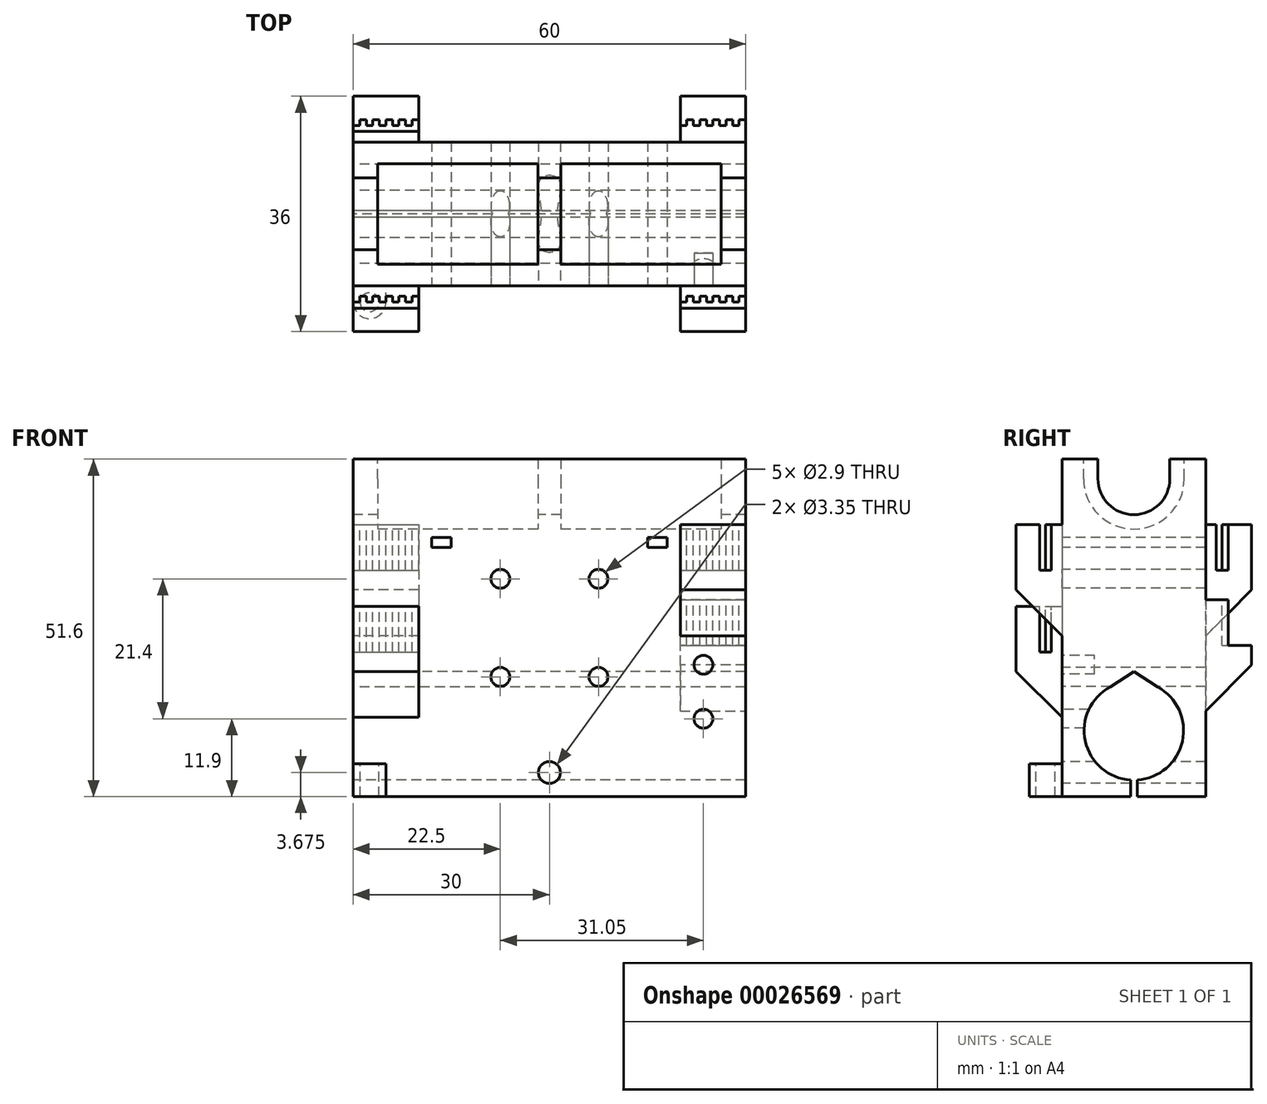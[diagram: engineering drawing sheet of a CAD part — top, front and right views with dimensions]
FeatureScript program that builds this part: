
annotation { "Feature Type Name" : "Feature", "Feature Type Description" : "" }
export const myFeature = defineFeature(function(context is Context, id is Id, definition is map)
    precondition{}
    {
        {
            var Q0;
            Q0=qCreatedBy(makeId("Top.planeOp"),FACE);
            var sketch = newSketch(context, id + "F0", { "sketchPlane" : qUnion([Q0])});
            skLineSegment(sketch, "E0.bottom", {"start": v(0, 0) * mm, "end": v(60, 0) * mm});
            skLineSegment(sketch, "E0.top", {"start": v(0, 22) * mm, "end": v(60, 22) * mm});
            skLineSegment(sketch, "E0.left", {"start": v(0, 0) * mm, "end": v(0, 22) * mm});
            skLineSegment(sketch, "E0.right", {"start": v(60, 0) * mm, "end": v(60, 22) * mm});
            skSolve(sketch);
        }
        {
            var Q0;
            Q0=qSketchRegion(id+"F0",true);
            extrude(context, id + "F1", {"entities" : qUnion([Q0]), "depth" : 51.6 * mm});
        }
        {
            var Q0;
            Q0=makeQuery(id+"F1.opExtrude","SWEPT_FACE",FACE,{"disambiguationData":[OSD([sQuery(id+"F0.wireOp",EDGE,"E0.left")])]});
            var sketch = newSketch(context, id + "F2", { "sketchPlane" : qUnion([Q0])});
            skCircle(sketch, "E1", {"center": v(-11, 10.1) * mm, "radius": 7.6 * mm});
            skCircle(sketch, "E2", {"center": v(-11, 48.6) * mm, "radius": 5.5 * mm});
            skLineSegment(sketch, "E3", {"start": v(-22, 48.6) * mm, "end": v(0, 48.6) * mm, "construction": true});
            skLineSegment(sketch, "E4", {"start": v(-16.5, 51.6) * mm, "end": v(-16.5, 48.6) * mm});
            skLineSegment(sketch, "E5", {"start": v(-5.5, 51.6) * mm, "end": v(-5.5, 48.6) * mm});
            skLineSegment(sketch, "E6", {"start": v(-22, 10.1) * mm, "end": v(0, 10.1) * mm, "construction": true});
            skLineSegment(sketch, "E7", {"start": v(-11, 10.1) * mm, "end": v(-11, 0) * mm, "construction": true});
            skLineSegment(sketch, "E8", {"start": v(-11, 0) * mm, "end": v(-11.5, 0) * mm});
            skLineSegment(sketch, "E9", {"start": v(-11.5, 0) * mm, "end": v(-11.5, 2.52) * mm});
            skLineSegment(sketch, "E10", {"start": v(-11.5, 2.52) * mm, "end": v(-10.5, 2.52) * mm});
            skLineSegment(sketch, "E11", {"start": v(-10.5, 2.52) * mm, "end": v(-10.5, 0) * mm});
            skLineSegment(sketch, "E12", {"start": v(-10.5, 0) * mm, "end": v(-11, 0) * mm});
            skLineSegment(sketch, "E13", {"start": v(-11, 17.7) * mm, "end": v(-11, 19.08) * mm});
            skLineSegment(sketch, "E14", {"start": v(-11, 19.08) * mm, "end": v(-6.5, 16.22) * mm});
            skLineSegment(sketch, "E15", {"start": v(-11, 19.08) * mm, "end": v(-15.5, 16.22) * mm});
            skCircle(sketch, "E16", {"center": v(-11, 48.6) * mm, "radius": 7.7 * mm});
            skLineSegment(sketch, "E17", {"start": v(-3.3, 48.6) * mm, "end": v(-3.3, 51.6) * mm});
            skLineSegment(sketch, "E18", {"start": v(-18.7, 48.6) * mm, "end": v(-18.7, 51.6) * mm});
            skSolve(sketch);
        }
        {
            var Q0;
            {var subQ0=sQuery(id+"F2.wireOp",EDGE,"E14");var subQ1=sQuery(id+"F2.wireOp",EDGE,"E1");var subQ3=makeQuery(id+"F2.imprint","INTERSECT",VERTEX,{"disambiguationData":[OD(0.0)],"derivedFrom":[subQ1,subQ0]});Q0=makeQuery(id+"F2.imprint","IMPRINT",FACE,{"disambiguationData":[TD([[makeQuery(id+"F2.imprint","IMPRINT",EDGE,{"disambiguationData":[TD([[subQ3,-1.0]])],"derivedFrom":subQ1}),1.0]])]});}
            var Q1;
            {var subQ0=sQuery(id+"F2.wireOp",EDGE,"E15");var subQ1=sQuery(id+"F2.wireOp",EDGE,"E1");var subQ3=makeQuery(id+"F2.imprint","INTERSECT",VERTEX,{"disambiguationData":[OD(0.0)],"derivedFrom":[subQ1,subQ0]});Q1=makeQuery(id+"F2.imprint","IMPRINT",FACE,{"disambiguationData":[TD([[makeQuery(id+"F2.imprint","IMPRINT",EDGE,{"disambiguationData":[TD([[subQ3,1.0]])],"derivedFrom":subQ1}),1.0]])]});}
            var Q2;
            Q2=makeQuery(id+"F2.imprint","IMPRINT",FACE,{"disambiguationData":[TD([[makeQuery(id+"F2.imprint","IMPRINT",EDGE,{"derivedFrom":sQuery(id+"F2.wireOp",EDGE,"E8")}),-1.0]])]});
            var Q3;
            {var subQ0=sQuery(id+"F2.wireOp",EDGE,"E10");Q3=makeQuery(id+"F2.imprint","IMPRINT",FACE,{"disambiguationData":[TD([[makeQuery(id+"F2.imprint","IMPRINT",EDGE,{"derivedFrom":subQ0}),-1.0]])]});}
            var Q4;
            {var subQ3=sQuery(id+"F2.wireOp",EDGE,"E13");Q4=makeQuery(id+"F2.imprint","IMPRINT",FACE,{"disambiguationData":[TD([[makeQuery(id+"F2.imprint","IMPRINT",EDGE,{"derivedFrom":subQ3}),-1.0]])]});}
            var Q5;
            {var subQ3=sQuery(id+"F2.wireOp",EDGE,"E13");Q5=makeQuery(id+"F2.imprint","IMPRINT",FACE,{"disambiguationData":[TD([[makeQuery(id+"F2.imprint","IMPRINT",EDGE,{"derivedFrom":subQ3}),1.0]])]});}
            var Q6;
            {var subQ7=sQuery(id+"F2.wireOp",EDGE,"E10");Q6=makeQuery(id+"F2.imprint","IMPRINT",FACE,{"disambiguationData":[TD([[makeQuery(id+"F2.imprint","IMPRINT",EDGE,{"derivedFrom":subQ7}),1.0]])]});}
            var Q7;
            {var subQ3=sQuery(id+"F2.wireOp",EDGE,"E5");Q7=makeQuery(id+"F2.imprint","IMPRINT",FACE,{"disambiguationData":[TD([[makeQuery(id+"F2.imprint","IMPRINT",EDGE,{"derivedFrom":subQ3}),-1.0]])]});}
            var Q8;
            {var subQ0=sQuery(id+"F2.wireOp",EDGE,"E4");Q8=makeQuery(id+"F2.imprint","IMPRINT",FACE,{"disambiguationData":[TD([[makeQuery(id+"F2.imprint","IMPRINT",EDGE,{"derivedFrom":subQ0}),1.0]])]});}
            var Q9;
            {var subQ0=sQuery(id+"F2.wireOp",EDGE,"E4");Q9=makeQuery(id+"F2.imprint","IMPRINT",FACE,{"disambiguationData":[TD([[makeQuery(id+"F2.imprint","IMPRINT",EDGE,{"derivedFrom":subQ0}),1.0]])]});}
            var Q10;
            {var subQ3=sQuery(id+"F2.wireOp",EDGE,"E5");Q10=makeQuery(id+"F2.imprint","IMPRINT",FACE,{"disambiguationData":[TD([[makeQuery(id+"F2.imprint","IMPRINT",EDGE,{"derivedFrom":subQ3}),-1.0]])]});}
            var Q11;
            {var subQ1=sQuery(id+"F2.wireOp",EDGE,"E2");var subQ4=makeQuery(id+"F2.imprint","INTERSECT",VERTEX,{"derivedFrom":[subQ1,sQuery(id+"F2.wireOp",EDGE,"E5")]});Q11=makeQuery(id+"F2.imprint","IMPRINT",FACE,{"disambiguationData":[TD([[makeQuery(id+"F2.imprint","IMPRINT",EDGE,{"disambiguationData":[TD([[subQ4,-1.0]])],"derivedFrom":subQ1}),1.0]])]});}
            extrude(context, id + "F3", {"entities" : qUnion([Q0, Q1, Q2, Q3, Q4, Q5, Q6, Q7, Q8, Q9, Q10, Q11]), "operationType" : NewBodyOperationType.REMOVE, "endBound" : BoundingType.THROUGH_ALL, "oppositeDirection" : true, "depth" : 25 * mm});
        }
        {
            var Q0;
            {var subQ3=sQuery(id+"F2.wireOp",EDGE,"E4");Q0=makeQuery(id+"F2.imprint","IMPRINT",FACE,{"disambiguationData":[TD([[makeQuery(id+"F2.imprint","IMPRINT",EDGE,{"derivedFrom":subQ3}),-1.0]])]});}
            var Q1;
            {var subQ3=sQuery(id+"F2.wireOp",EDGE,"E18");Q1=makeQuery(id+"F2.imprint","IMPRINT",FACE,{"disambiguationData":[TD([[makeQuery(id+"F2.imprint","IMPRINT",EDGE,{"derivedFrom":subQ3}),-1.0]])]});}
            var Q2;
            {var subQ3=sQuery(id+"F2.wireOp",EDGE,"E17");Q2=makeQuery(id+"F2.imprint","IMPRINT",FACE,{"disambiguationData":[TD([[makeQuery(id+"F2.imprint","IMPRINT",EDGE,{"derivedFrom":subQ3}),1.0]])]});}
            extrude(context, id + "F4", {"entities" : qUnion([Q0, Q1, Q2]), "operationType" : NewBodyOperationType.REMOVE, "oppositeDirection" : true, "depth" : 56.25 * mm});
        }
        {
            var Q0;
            {var subQ3=sQuery(id+"F2.wireOp",EDGE,"E4");Q0=makeQuery(id+"F2.imprint","IMPRINT",FACE,{"disambiguationData":[TD([[makeQuery(id+"F2.imprint","IMPRINT",EDGE,{"derivedFrom":subQ3}),-1.0]])]});}
            var Q1;
            {var subQ3=sQuery(id+"F2.wireOp",EDGE,"E18");Q1=makeQuery(id+"F2.imprint","IMPRINT",FACE,{"disambiguationData":[TD([[makeQuery(id+"F2.imprint","IMPRINT",EDGE,{"derivedFrom":subQ3}),-1.0]])]});}
            var Q2;
            {var subQ3=sQuery(id+"F2.wireOp",EDGE,"E17");Q2=makeQuery(id+"F2.imprint","IMPRINT",FACE,{"disambiguationData":[TD([[makeQuery(id+"F2.imprint","IMPRINT",EDGE,{"derivedFrom":subQ3}),1.0]])]});}
            extrude(context, id + "F5", {"entities" : qUnion([Q0, Q1, Q2]), "operationType" : NewBodyOperationType.ADD, "oppositeDirection" : true, "depth" : 31.75 * mm});
        }
        {
            var Q0;
            {var subQ3=sQuery(id+"F2.wireOp",EDGE,"E4");Q0=makeQuery(id+"F2.imprint","IMPRINT",FACE,{"disambiguationData":[TD([[makeQuery(id+"F2.imprint","IMPRINT",EDGE,{"derivedFrom":subQ3}),-1.0]])]});}
            var Q1;
            {var subQ3=sQuery(id+"F2.wireOp",EDGE,"E18");Q1=makeQuery(id+"F2.imprint","IMPRINT",FACE,{"disambiguationData":[TD([[makeQuery(id+"F2.imprint","IMPRINT",EDGE,{"derivedFrom":subQ3}),-1.0]])]});}
            var Q2;
            {var subQ3=sQuery(id+"F2.wireOp",EDGE,"E17");Q2=makeQuery(id+"F2.imprint","IMPRINT",FACE,{"disambiguationData":[TD([[makeQuery(id+"F2.imprint","IMPRINT",EDGE,{"derivedFrom":subQ3}),1.0]])]});}
            extrude(context, id + "F6", {"entities" : qUnion([Q0, Q1, Q2]), "operationType" : NewBodyOperationType.REMOVE, "oppositeDirection" : true, "depth" : 28.25 * mm});
        }
        {
            var Q0;
            {var subQ3=sQuery(id+"F2.wireOp",EDGE,"E4");Q0=makeQuery(id+"F2.imprint","IMPRINT",FACE,{"disambiguationData":[TD([[makeQuery(id+"F2.imprint","IMPRINT",EDGE,{"derivedFrom":subQ3}),-1.0]])]});}
            var Q1;
            {var subQ3=sQuery(id+"F2.wireOp",EDGE,"E18");Q1=makeQuery(id+"F2.imprint","IMPRINT",FACE,{"disambiguationData":[TD([[makeQuery(id+"F2.imprint","IMPRINT",EDGE,{"derivedFrom":subQ3}),-1.0]])]});}
            var Q2;
            {var subQ3=sQuery(id+"F2.wireOp",EDGE,"E17");Q2=makeQuery(id+"F2.imprint","IMPRINT",FACE,{"disambiguationData":[TD([[makeQuery(id+"F2.imprint","IMPRINT",EDGE,{"derivedFrom":subQ3}),1.0]])]});}
            extrude(context, id + "F7", {"entities" : qUnion([Q0, Q1, Q2]), "operationType" : NewBodyOperationType.ADD, "oppositeDirection" : true, "depth" : 3.75 * mm});
        }
        {
            var Q0;
            Q0=makeQuery(id+"F1.opExtrude","SWEPT_FACE",FACE,{"disambiguationData":[OSD([sQuery(id+"F0.wireOp",EDGE,"E0.bottom")])]});
            var sketch = newSketch(context, id + "F8", { "sketchPlane" : qUnion([Q0])});
            skLineSegment(sketch, "E19.bottom", {"start": v(0, 29.1) * mm, "end": v(10, 29.1) * mm});
            skLineSegment(sketch, "E19.top", {"start": v(0, 9.1) * mm, "end": v(10, 9.1) * mm});
            skLineSegment(sketch, "E19.left", {"start": v(0, 29.1) * mm, "end": v(0, 9.1) * mm});
            skLineSegment(sketch, "E19.right", {"start": v(10, 29.1) * mm, "end": v(10, 9.1) * mm});
            skLineSegment(sketch, "E20.bottom", {"start": v(60, 41.6) * mm, "end": v(50, 41.6) * mm});
            skLineSegment(sketch, "E20.top", {"start": v(60, 21.6) * mm, "end": v(50, 21.6) * mm});
            skLineSegment(sketch, "E20.left", {"start": v(60, 41.6) * mm, "end": v(60, 21.6) * mm});
            skLineSegment(sketch, "E20.right", {"start": v(50, 41.6) * mm, "end": v(50, 21.6) * mm});
            skPoint(sketch, "E21", {"position": v(0, 48.6) * mm});
            skPoint(sketch, "E22", {"position": v(0, 8.6) * mm});
            skSolve(sketch);
        }
        {
            var Q0;
            Q0=qSketchRegion(id+"F8",true);
            extrude(context, id + "F9", {"entities" : qUnion([Q0]), "operationType" : NewBodyOperationType.ADD, "depth" : 7 * mm});
        }
        {
            var Q0;
            Q0=makeQuery(id+"F9.opExtrude","CAP_EDGE",EDGE,{"disambiguationData":[OSD([sQuery(id+"F8.wireOp",EDGE,"E19.top")])],"isStart":false});
            var Q1;
            Q1=makeQuery(id+"F9.opExtrude","CAP_EDGE",EDGE,{"disambiguationData":[OSD([sQuery(id+"F8.wireOp",EDGE,"E20.top")])],"isStart":false});
            chamfer(context, id + "F10", {"entities" : qUnion([Q0, Q1]), "width" : 10 * mm, "tangentPropagation" : true});
        }
        {
            var Q0;
            Q0=makeQuery(id+"F9.opExtrude","SWEPT_FACE",FACE,{"disambiguationData":[OSD([sQuery(id+"F8.wireOp",EDGE,"E19.bottom")])]});
            var sketch = newSketch(context, id + "F11", { "sketchPlane" : qUnion([Q0])});
            skLineSegment(sketch, "E23", {"start": v(-935.9, 0) * mm, "end": v(-935.88, -4.54) * mm});
            skLineSegment(sketch, "E24.left", {"start": v(0, -3.4) * mm, "end": v(0, -1.6) * mm});
            skLineSegment(sketch, "E25", {"start": v(6, -2.5) * mm, "end": v(7, -2.5) * mm});
            skLineSegment(sketch, "E26", {"start": v(4, -2.5) * mm, "end": v(5, -2.5) * mm});
            skLineSegment(sketch, "E27", {"start": v(0, -2.5) * mm, "end": v(1, -2.5) * mm});
            skLineSegment(sketch, "E28", {"start": v(7, -1.6) * mm, "end": v(8, -1.6) * mm});
            skLineSegment(sketch, "E29", {"start": v(2, -2.5) * mm, "end": v(3, -2.5) * mm});
            skLineSegment(sketch, "E30", {"start": v(3, -1.6) * mm, "end": v(4, -1.6) * mm});
            skLineSegment(sketch, "E31", {"start": v(8, -2.5) * mm, "end": v(9, -2.5) * mm});
            skLineSegment(sketch, "E32", {"start": v(8, -1.6) * mm, "end": v(8, -2.5) * mm});
            skLineSegment(sketch, "E33", {"start": v(9, -2.5) * mm, "end": v(9, -1.6) * mm});
            skLineSegment(sketch, "E34", {"start": v(10, -1.6) * mm, "end": v(10, -2.5) * mm});
            skLineSegment(sketch, "E35", {"start": v(6, -1.6) * mm, "end": v(6, -2.5) * mm});
            skLineSegment(sketch, "E36", {"start": v(2, -1.6) * mm, "end": v(2, -2.5) * mm});
            skLineSegment(sketch, "E37", {"start": v(1, -1.6) * mm, "end": v(2, -1.6) * mm});
            skLineSegment(sketch, "E38", {"start": v(1, -2.5) * mm, "end": v(1, -1.6) * mm});
            skLineSegment(sketch, "E39", {"start": v(9, -1.6) * mm, "end": v(10, -1.6) * mm});
            skLineSegment(sketch, "E40", {"start": v(5, -1.6) * mm, "end": v(6, -1.6) * mm});
            skLineSegment(sketch, "E41", {"start": v(5, -2.5) * mm, "end": v(5, -1.6) * mm});
            skLineSegment(sketch, "E42", {"start": v(3, -2.5) * mm, "end": v(3, -1.6) * mm});
            skLineSegment(sketch, "E43", {"start": v(4, -1.6) * mm, "end": v(4, -2.5) * mm});
            skLineSegment(sketch, "E44", {"start": v(7, -2.5) * mm, "end": v(7, -1.6) * mm});
            skLineSegment(sketch, "E45", {"start": v(0, -1.6) * mm, "end": v(0, -2.5) * mm});
            skLineSegment(sketch, "E46", {"start": v(10, -2.5) * mm, "end": v(10, -3.4) * mm});
            skLineSegment(sketch, "E47", {"start": v(0, -3.4) * mm, "end": v(10, -3.4) * mm});
            skLineSegment(sketch, "E48", {"start": v(5.3, -1.6) * mm, "end": v(5.3, 0) * mm});
            skSolve(sketch);
        }
        {
            var Q0;
            Q0=qSketchRegion(id+"F11",true);
            extrude(context, id + "F12", {"entities" : qUnion([Q0]), "operationType" : NewBodyOperationType.REMOVE, "oppositeDirection" : true, "depth" : 7 * mm});
        }
        {
            var Q0;
            Q0=makeQuery(id+"F9.opExtrude","SWEPT_FACE",FACE,{"disambiguationData":[OSD([sQuery(id+"F8.wireOp",EDGE,"E20.bottom")])]});
            var sketch = newSketch(context, id + "F13", { "sketchPlane" : qUnion([Q0])});
            skLineSegment(sketch, "E49.left", {"start": v(50, -3.4) * mm, "end": v(50, -1.6) * mm});
            skLineSegment(sketch, "E50", {"start": v(56, -2.5) * mm, "end": v(57, -2.5) * mm});
            skLineSegment(sketch, "E51", {"start": v(54, -2.5) * mm, "end": v(55, -2.5) * mm});
            skLineSegment(sketch, "E52", {"start": v(50, -2.5) * mm, "end": v(51, -2.5) * mm});
            skLineSegment(sketch, "E53", {"start": v(57, -1.6) * mm, "end": v(58, -1.6) * mm});
            skLineSegment(sketch, "E54", {"start": v(52, -2.5) * mm, "end": v(53, -2.5) * mm});
            skLineSegment(sketch, "E55", {"start": v(53, -1.6) * mm, "end": v(54, -1.6) * mm});
            skLineSegment(sketch, "E56", {"start": v(58, -2.5) * mm, "end": v(59, -2.5) * mm});
            skLineSegment(sketch, "E57", {"start": v(58, -1.6) * mm, "end": v(58, -2.5) * mm});
            skLineSegment(sketch, "E58", {"start": v(59, -2.5) * mm, "end": v(59, -1.6) * mm});
            skLineSegment(sketch, "E59", {"start": v(60, -1.6) * mm, "end": v(60, -2.5) * mm});
            skLineSegment(sketch, "E60", {"start": v(56, -1.6) * mm, "end": v(56, -2.5) * mm});
            skLineSegment(sketch, "E61", {"start": v(52, -1.6) * mm, "end": v(52, -2.5) * mm});
            skLineSegment(sketch, "E62", {"start": v(51, -1.6) * mm, "end": v(52, -1.6) * mm});
            skLineSegment(sketch, "E63", {"start": v(51, -2.5) * mm, "end": v(51, -1.6) * mm});
            skLineSegment(sketch, "E64", {"start": v(59, -1.6) * mm, "end": v(60, -1.6) * mm});
            skLineSegment(sketch, "E65", {"start": v(55, -1.6) * mm, "end": v(56, -1.6) * mm});
            skLineSegment(sketch, "E66", {"start": v(55, -2.5) * mm, "end": v(55, -1.6) * mm});
            skLineSegment(sketch, "E67", {"start": v(53, -2.5) * mm, "end": v(53, -1.6) * mm});
            skLineSegment(sketch, "E68", {"start": v(54, -1.6) * mm, "end": v(54, -2.5) * mm});
            skLineSegment(sketch, "E69", {"start": v(57, -2.5) * mm, "end": v(57, -1.6) * mm});
            skLineSegment(sketch, "E70", {"start": v(50, -1.6) * mm, "end": v(50, -2.5) * mm});
            skLineSegment(sketch, "E71", {"start": v(60, -2.5) * mm, "end": v(60, -3.4) * mm});
            skLineSegment(sketch, "E72", {"start": v(50, -3.4) * mm, "end": v(60, -3.4) * mm});
            skLineSegment(sketch, "E73", {"start": v(55.23, -1.6) * mm, "end": v(55.23, 0) * mm});
            skSolve(sketch);
        }
        {
            var Q0;
            Q0=qSketchRegion(id+"F13",true);
            extrude(context, id + "F14", {"entities" : qUnion([Q0]), "operationType" : NewBodyOperationType.REMOVE, "oppositeDirection" : true, "depth" : 7 * mm});
        }
        {
            var Q0;
            Q0=makeQuery(id+"F1.opExtrude","SWEPT_FACE",FACE,{"disambiguationData":[OSD([sQuery(id+"F0.wireOp",EDGE,"E0.top")])]});
            var sketch = newSketch(context, id + "F15", { "sketchPlane" : qUnion([Q0])});
            skLineSegment(sketch, "E74.bottom", {"start": v(-60, 10.1) * mm, "end": v(-50, 10.1) * mm});
            skLineSegment(sketch, "E74.top", {"start": v(-60, 30.1) * mm, "end": v(-50, 30.1) * mm});
            skLineSegment(sketch, "E74.left", {"start": v(-60, 10.1) * mm, "end": v(-60, 30.1) * mm});
            skLineSegment(sketch, "E74.right", {"start": v(-50, 10.1) * mm, "end": v(-50, 30.1) * mm});
            skLineSegment(sketch, "E75.bottom", {"start": v(0, 41.6) * mm, "end": v(-10, 41.6) * mm});
            skLineSegment(sketch, "E75.top", {"start": v(0, 21.6) * mm, "end": v(-10, 21.6) * mm});
            skLineSegment(sketch, "E75.left", {"start": v(0, 41.6) * mm, "end": v(0, 21.6) * mm});
            skLineSegment(sketch, "E75.right", {"start": v(-10, 41.6) * mm, "end": v(-10, 21.6) * mm});
            skSolve(sketch);
        }
        {
            var Q0;
            Q0=qSketchRegion(id+"F15",true);
            extrude(context, id + "F16", {"entities" : qUnion([Q0]), "operationType" : NewBodyOperationType.ADD, "depth" : 7 * mm});
        }
        {
            var Q0;
            Q0=makeQuery(id+"F16.opExtrude","SWEPT_FACE",FACE,{"disambiguationData":[OSD([sQuery(id+"F15.wireOp",EDGE,"E74.top")])]});
            var sketch = newSketch(context, id + "F17", { "sketchPlane" : qUnion([Q0])});
            skLineSegment(sketch, "E76.left", {"start": v(50, 23.6) * mm, "end": v(50, 25.4) * mm});
            skLineSegment(sketch, "E77", {"start": v(56, 24.5) * mm, "end": v(57, 24.5) * mm});
            skLineSegment(sketch, "E78", {"start": v(54, 24.5) * mm, "end": v(55, 24.5) * mm});
            skLineSegment(sketch, "E79", {"start": v(50, 24.5) * mm, "end": v(51, 24.5) * mm});
            skLineSegment(sketch, "E80", {"start": v(57, 25.4) * mm, "end": v(58, 25.4) * mm});
            skLineSegment(sketch, "E81", {"start": v(52, 24.5) * mm, "end": v(53, 24.5) * mm});
            skLineSegment(sketch, "E82", {"start": v(53, 25.4) * mm, "end": v(54, 25.4) * mm});
            skLineSegment(sketch, "E83", {"start": v(58, 24.5) * mm, "end": v(59, 24.5) * mm});
            skLineSegment(sketch, "E84", {"start": v(58, 25.4) * mm, "end": v(58, 24.5) * mm});
            skLineSegment(sketch, "E85", {"start": v(59, 24.5) * mm, "end": v(59, 25.4) * mm});
            skLineSegment(sketch, "E86", {"start": v(60, 25.4) * mm, "end": v(60, 24.5) * mm});
            skLineSegment(sketch, "E87", {"start": v(56, 25.4) * mm, "end": v(56, 24.5) * mm});
            skLineSegment(sketch, "E88", {"start": v(52, 25.4) * mm, "end": v(52, 24.5) * mm});
            skLineSegment(sketch, "E89", {"start": v(51, 25.4) * mm, "end": v(52, 25.4) * mm});
            skLineSegment(sketch, "E90", {"start": v(51, 24.5) * mm, "end": v(51, 25.4) * mm});
            skLineSegment(sketch, "E91", {"start": v(59, 25.4) * mm, "end": v(60, 25.4) * mm});
            skLineSegment(sketch, "E92", {"start": v(55, 25.4) * mm, "end": v(56, 25.4) * mm});
            skLineSegment(sketch, "E93", {"start": v(55, 24.5) * mm, "end": v(55, 25.4) * mm});
            skLineSegment(sketch, "E94", {"start": v(53, 24.5) * mm, "end": v(53, 25.4) * mm});
            skLineSegment(sketch, "E95", {"start": v(54, 25.4) * mm, "end": v(54, 24.5) * mm});
            skLineSegment(sketch, "E96", {"start": v(57, 24.5) * mm, "end": v(57, 25.4) * mm});
            skLineSegment(sketch, "E97", {"start": v(50, 25.4) * mm, "end": v(50, 24.5) * mm});
            skLineSegment(sketch, "E98", {"start": v(60, 24.5) * mm, "end": v(60, 23.6) * mm});
            skLineSegment(sketch, "E99", {"start": v(50, 23.6) * mm, "end": v(60, 23.6) * mm});
            skLineSegment(sketch, "E100", {"start": v(55, 23.6) * mm, "end": v(55, 22) * mm});
            skSolve(sketch);
        }
        {
            var Q0;
            {var subQ4=sQuery(id+"F17.wireOp",EDGE,"E76.left");Q0=makeQuery(id+"F17.imprint","IMPRINT",FACE,{"disambiguationData":[TD([[makeQuery(id+"F17.imprint","IMPRINT",EDGE,{"derivedFrom":subQ4}),1.0]])]});}
            extrude(context, id + "F18", {"entities" : qUnion([Q0]), "operationType" : NewBodyOperationType.REMOVE, "oppositeDirection" : true, "depth" : 7 * mm});
        }
        {
            var Q0;
            Q0=makeQuery(id+"F16.opExtrude","SWEPT_FACE",FACE,{"disambiguationData":[OSD([sQuery(id+"F15.wireOp",EDGE,"E75.bottom")])]});
            var sketch = newSketch(context, id + "F19", { "sketchPlane" : qUnion([Q0])});
            skLineSegment(sketch, "E101", {"start": v(6, 24.5) * mm, "end": v(7, 24.5) * mm});
            skLineSegment(sketch, "E102", {"start": v(4, 24.5) * mm, "end": v(5, 24.5) * mm});
            skLineSegment(sketch, "E103", {"start": v(0, 24.5) * mm, "end": v(1, 24.5) * mm});
            skLineSegment(sketch, "E104", {"start": v(7, 25.4) * mm, "end": v(8, 25.4) * mm});
            skLineSegment(sketch, "E105", {"start": v(2, 24.5) * mm, "end": v(3, 24.5) * mm});
            skLineSegment(sketch, "E106", {"start": v(3, 25.4) * mm, "end": v(4, 25.4) * mm});
            skLineSegment(sketch, "E107", {"start": v(8, 24.5) * mm, "end": v(9, 24.5) * mm});
            skLineSegment(sketch, "E108", {"start": v(8, 25.4) * mm, "end": v(8, 24.5) * mm});
            skLineSegment(sketch, "E109", {"start": v(9, 24.5) * mm, "end": v(9, 25.4) * mm});
            skLineSegment(sketch, "E110", {"start": v(10, 25.4) * mm, "end": v(10, 24.5) * mm});
            skLineSegment(sketch, "E111", {"start": v(6, 25.4) * mm, "end": v(6, 24.5) * mm});
            skLineSegment(sketch, "E112", {"start": v(2, 25.4) * mm, "end": v(2, 24.5) * mm});
            skLineSegment(sketch, "E113", {"start": v(1, 25.4) * mm, "end": v(2, 25.4) * mm});
            skLineSegment(sketch, "E114", {"start": v(1, 24.5) * mm, "end": v(1, 25.4) * mm});
            skLineSegment(sketch, "E115", {"start": v(9, 25.4) * mm, "end": v(10, 25.4) * mm});
            skLineSegment(sketch, "E116", {"start": v(5, 25.4) * mm, "end": v(6, 25.4) * mm});
            skLineSegment(sketch, "E117", {"start": v(5, 24.5) * mm, "end": v(5, 25.4) * mm});
            skLineSegment(sketch, "E118", {"start": v(3, 24.5) * mm, "end": v(3, 25.4) * mm});
            skLineSegment(sketch, "E119", {"start": v(4, 25.4) * mm, "end": v(4, 24.5) * mm});
            skLineSegment(sketch, "E120", {"start": v(7, 24.5) * mm, "end": v(7, 25.4) * mm});
            skLineSegment(sketch, "E121", {"start": v(10, 24.5) * mm, "end": v(10, 23.6) * mm});
            skLineSegment(sketch, "E122", {"start": v(0, 23.6) * mm, "end": v(10, 23.6) * mm});
            skLineSegment(sketch, "E123", {"start": v(5, 23.6) * mm, "end": v(5, 22) * mm});
            skLineSegment(sketch, "E124", {"start": v(0, 23.6) * mm, "end": v(0, 24.5) * mm});
            skSolve(sketch);
        }
        {
            var Q0;
            Q0=makeQuery(id+"F19.imprint","IMPRINT",FACE,{"disambiguationData":[TD([[makeQuery(id+"F19.imprint","IMPRINT",EDGE,{"derivedFrom":sQuery(id+"F19.wireOp",EDGE,"E101")}),-1.0]])]});
            extrude(context, id + "F20", {"entities" : qUnion([Q0]), "operationType" : NewBodyOperationType.REMOVE, "oppositeDirection" : true, "depth" : 7 * mm});
        }
        {
            var Q0;
            Q0=makeQuery(id+"F16.opExtrude","CAP_EDGE",EDGE,{"disambiguationData":[OSD([sQuery(id+"F15.wireOp",EDGE,"E75.top")])],"isStart":false});
            var Q1;
            Q1=makeQuery(id+"F16.opExtrude","CAP_EDGE",EDGE,{"disambiguationData":[OSD([sQuery(id+"F15.wireOp",EDGE,"E74.bottom")])],"isStart":false});
            chamfer(context, id + "F21", {"entities" : qUnion([Q0, Q1]), "width" : 10 * mm, "tangentPropagation" : true});
        }
        {
            var Q0;
            Q0=makeQuery(id+"F1.opExtrude","SWEPT_FACE",FACE,{"disambiguationData":[OSD([sQuery(id+"F0.wireOp",EDGE,"E0.bottom")])]});
            var sketch = newSketch(context, id + "F22", { "sketchPlane" : qUnion([Q0])});
            skCircle(sketch, "E125", {"center": v(22.5, 33.3) * mm, "radius": 1.45 * mm});
            skCircle(sketch, "E126", {"center": v(37.5, 33.3) * mm, "radius": 1.45 * mm});
            skCircle(sketch, "E127", {"center": v(22.5, 18.3) * mm, "radius": 1.45 * mm});
            skCircle(sketch, "E128", {"center": v(37.5, 18.3) * mm, "radius": 1.45 * mm});
            skLineSegment(sketch, "E129", {"start": v(22.5, 33.3) * mm, "end": v(0, 33.3) * mm});
            skLineSegment(sketch, "E130", {"start": v(37.5, 18.3) * mm, "end": v(60, 18.3) * mm});
            skLineSegment(sketch, "E131", {"start": v(37.5, 33.3) * mm, "end": v(37.5, 51.6) * mm});
            skLineSegment(sketch, "E132", {"start": v(22.5, 18.3) * mm, "end": v(22.5, 0) * mm});
            skCircle(sketch, "E133", {"center": v(30, 3.68) * mm, "radius": 1.68 * mm});
            skLineSegment(sketch, "E134", {"start": v(30, 0) * mm, "end": v(30, 13.82) * mm, "construction": true});
            skSolve(sketch);
        }
        {
            var Q0;
            Q0=qSketchRegion(id+"F22",true);
            var Q1;
            Q1=makeQuery(id+"F22.imprint","IMPRINT",FACE,{"disambiguationData":[TD([[makeQuery(id+"F22.imprint","IMPRINT",EDGE,{"derivedFrom":sQuery(id+"F22.wireOp",EDGE,"E125")}),1.0]])]});
            var Q2;
            Q2=makeQuery(id+"F22.imprint","IMPRINT",FACE,{"disambiguationData":[TD([[makeQuery(id+"F22.imprint","IMPRINT",EDGE,{"derivedFrom":sQuery(id+"F22.wireOp",EDGE,"E126")}),1.0]])]});
            var Q3;
            Q3=makeQuery(id+"F22.imprint","IMPRINT",FACE,{"disambiguationData":[TD([[makeQuery(id+"F22.imprint","IMPRINT",EDGE,{"derivedFrom":sQuery(id+"F22.wireOp",EDGE,"E128")}),1.0]])]});
            var Q4;
            Q4=makeQuery(id+"F22.imprint","IMPRINT",FACE,{"disambiguationData":[TD([[makeQuery(id+"F22.imprint","IMPRINT",EDGE,{"derivedFrom":sQuery(id+"F22.wireOp",EDGE,"E127")}),1.0]])]});
            extrude(context, id + "F23", {"entities" : qUnion([Q0, Q1, Q2, Q3, Q4]), "operationType" : NewBodyOperationType.REMOVE, "endBound" : BoundingType.THROUGH_ALL, "oppositeDirection" : true, "depth" : 25 * mm});
        }
        {
            var Q0;
            Q0=makeQuery(id+"F1.opExtrude","SWEPT_FACE",FACE,{"disambiguationData":[OSD([sQuery(id+"F0.wireOp",EDGE,"E0.bottom")])]});
            var sketch = newSketch(context, id + "F24", { "sketchPlane" : qUnion([Q0])});
            skCircle(sketch, "E135", {"center": v(53.55, 20.15) * mm, "radius": 1.45 * mm});
            skCircle(sketch, "E136", {"center": v(53.55, 11.9) * mm, "radius": 1.45 * mm});
            skSolve(sketch);
        }
        {
            var Q0;
            Q0=qSketchRegion(id+"F24",true);
            extrude(context, id + "F25", {"entities" : qUnion([Q0]), "operationType" : NewBodyOperationType.REMOVE, "oppositeDirection" : true, "depth" : 5 * mm});
        }
        {
            var Q0;
            Q0=makeQuery(id+"F1.opExtrude","SWEPT_FACE",FACE,{"disambiguationData":[OSD([sQuery(id+"F0.wireOp",EDGE,"E0.bottom")])]});
            var sketch = newSketch(context, id + "F26", { "sketchPlane" : qUnion([Q0])});
            skText(sketch, "E137", { "text": "F", "fontName": "OpenSans-Bold.ttf"});
            skLineSegment(sketch, "E138", {"start": v(22.5, 33.3) * mm, "end": v(22.5, 18.3) * mm, "construction": true});
            skLineSegment(sketch, "E139", {"start": v(22.5, 18.3) * mm, "end": v(37.5, 18.3) * mm, "construction": true});
            skLineSegment(sketch, "E140", {"start": v(37.5, 18.3) * mm, "end": v(37.5, 33.3) * mm, "construction": true});
            skLineSegment(sketch, "E141", {"start": v(37.5, 33.3) * mm, "end": v(22.5, 33.3) * mm, "construction": true});
            skLineSegment(sketch, "E142", {"start": v(22.5, 25.8) * mm, "end": v(25.4, 25.8) * mm, "construction": true});
            skLineSegment(sketch, "E143", {"start": v(34.6, 25.8) * mm, "end": v(37.5, 25.8) * mm, "construction": true});
            skLineSegment(sketch, "E144", {"start": v(30, 19.16) * mm, "end": v(30, 18.3) * mm, "construction": true});
            skLineSegment(sketch, "E145", {"start": v(30, 33.3) * mm, "end": v(30, 32.44) * mm, "construction": true});
            const initialGuessF26  = {"E137": [0.0204, 0.01866, 1, 0, 0.01328]};
            skSetInitialGuess(sketch, initialGuessF26);
            skSolve(sketch);
        }
        {
            var Q0;
            Q0=makeQuery(id+"F1.opExtrude","SWEPT_FACE",FACE,{"disambiguationData":[OSD([sQuery(id+"F0.wireOp",EDGE,"E0.bottom")])]});
            var sketch = newSketch(context, id + "F27", { "sketchPlane" : qUnion([Q0])});
            skLineSegment(sketch, "E146.bottom", {"start": v(0, 0) * mm, "end": v(5, 0) * mm});
            skLineSegment(sketch, "E146.top", {"start": v(0, 5) * mm, "end": v(5, 5) * mm});
            skLineSegment(sketch, "E146.left", {"start": v(0, 0) * mm, "end": v(0, 5) * mm});
            skLineSegment(sketch, "E146.right", {"start": v(5, 0) * mm, "end": v(5, 5) * mm});
            skSolve(sketch);
        }
        {
            var Q0;
            Q0=qSketchRegion(id+"F27",true);
            extrude(context, id + "F28", {"entities" : qUnion([Q0]), "operationType" : NewBodyOperationType.ADD, "depth" : 5 * mm});
        }
        {
            var Q0;
            Q0=makeQuery(id+"F28.opExtrude","SWEPT_FACE",FACE,{"disambiguationData":[OSD([sQuery(id+"F27.wireOp",EDGE,"E146.top")])]});
            var sketch = newSketch(context, id + "F29", { "sketchPlane" : qUnion([Q0])});
            skCircle(sketch, "E147", {"center": v(2.5, -2.5) * mm, "radius": 1.45 * mm});
            skLineSegment(sketch, "E148", {"start": v(0, -2.5) * mm, "end": v(5, -2.5) * mm});
            skSolve(sketch);
        }
        {
            var Q0;
            Q0=qSketchRegion(id+"F29",true);
            extrude(context, id + "F30", {"entities" : qUnion([Q0]), "operationType" : NewBodyOperationType.REMOVE, "oppositeDirection" : true, "depth" : 25 * mm});
        }
        {
            var Q0;
            Q0=makeQuery(id+"F28.opExtrude","CAP_EDGE",EDGE,{"disambiguationData":[OSD([sQuery(id+"F27.wireOp",EDGE,"E146.left")])],"isStart":false});
            var Q1;
            Q1=makeQuery(id+"F28.opExtrude","CAP_EDGE",EDGE,{"disambiguationData":[OSD([sQuery(id+"F27.wireOp",EDGE,"E146.right")])],"isStart":false});
            fillet(context, id + "F31", {"entities" : qUnion([Q0, Q1]), "radius" : 2.5 * mm, "tangentPropagation" : true, "allowEdgeOverflow" : false});
        }
        {
            var Q0;
            Q0=makeQuery(id+"F1.opExtrude","SWEPT_FACE",FACE,{"disambiguationData":[OSD([sQuery(id+"F0.wireOp",EDGE,"E0.bottom")])]});
            var sketch = newSketch(context, id + "F32", { "sketchPlane" : qUnion([Q0])});
            skLineSegment(sketch, "E149.bottom", {"start": v(12, 39.6) * mm, "end": v(15, 39.6) * mm});
            skLineSegment(sketch, "E149.top", {"start": v(12, 38.1) * mm, "end": v(15, 38.1) * mm});
            skLineSegment(sketch, "E149.left", {"start": v(12, 39.6) * mm, "end": v(12, 38.1) * mm});
            skLineSegment(sketch, "E149.right", {"start": v(15, 39.6) * mm, "end": v(15, 38.1) * mm});
            skLineSegment(sketch, "E150", {"start": v(30, 51.6) * mm, "end": v(30, 35.77) * mm, "construction": true});
            skLineSegment(sketch, "E151.MirrorCS", {"start": v(48, 39.6) * mm, "end": v(48, 38.1) * mm});
            skLineSegment(sketch, "E152.MirrorCS", {"start": v(45, 39.6) * mm, "end": v(45, 38.1) * mm});
            skLineSegment(sketch, "E153.MirrorCS", {"start": v(48, 39.6) * mm, "end": v(45, 39.6) * mm});
            skLineSegment(sketch, "E154.MirrorCS", {"start": v(48, 38.1) * mm, "end": v(45, 38.1) * mm});
            skSolve(sketch);
        }
        {
            var Q0;
            Q0=makeQuery(id+"F32.imprint","IMPRINT",FACE,{"disambiguationData":[TD([[makeQuery(id+"F32.imprint","IMPRINT",EDGE,{"derivedFrom":sQuery(id+"F32.wireOp",EDGE,"E149.bottom")}),-1.0]])]});
            var Q1;
            Q1=makeQuery(id+"F32.imprint","IMPRINT",FACE,{"disambiguationData":[TD([[makeQuery(id+"F32.imprint","IMPRINT",EDGE,{"derivedFrom":sQuery(id+"F32.wireOp",EDGE,"E151.MirrorCS")}),-1.0]])]});
            extrude(context, id + "F33", {"entities" : qUnion([Q0, Q1]), "operationType" : NewBodyOperationType.REMOVE, "endBound" : BoundingType.THROUGH_ALL, "oppositeDirection" : true, "depth" : 25 * mm});
        }
    });
